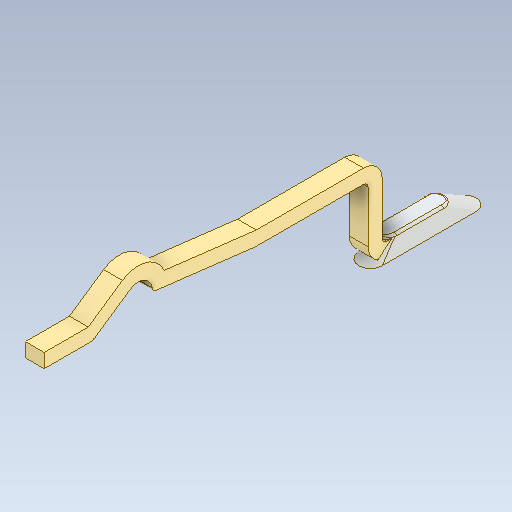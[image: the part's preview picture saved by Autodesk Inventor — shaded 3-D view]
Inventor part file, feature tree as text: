
AUTODESK INVENTOR PART (.ipt)
format: ipt  version: 2020 (Build 240168000, 168)  size: 163,328 bytes
history: native  units: in
note: dims shown in document units (in); Inventor stores cm internally (conversion verified against a paired STEP export)
features: fillet x1
ambient origin geometry x8: Origin, YZ Plane, XZ Plane, XY Plane, X Axis, Y Axis, Z Axis, Center Point
bodies: Solid1 (feature_tree)
feature tree (1):
  fillet  "Fillet2"  [1 undecoded]
note: 1 required parameter value undecoded (feature->parameter linkage not recoverable at this tier; creation-order binding heuristic only, values carry confidence <= 0.55)
